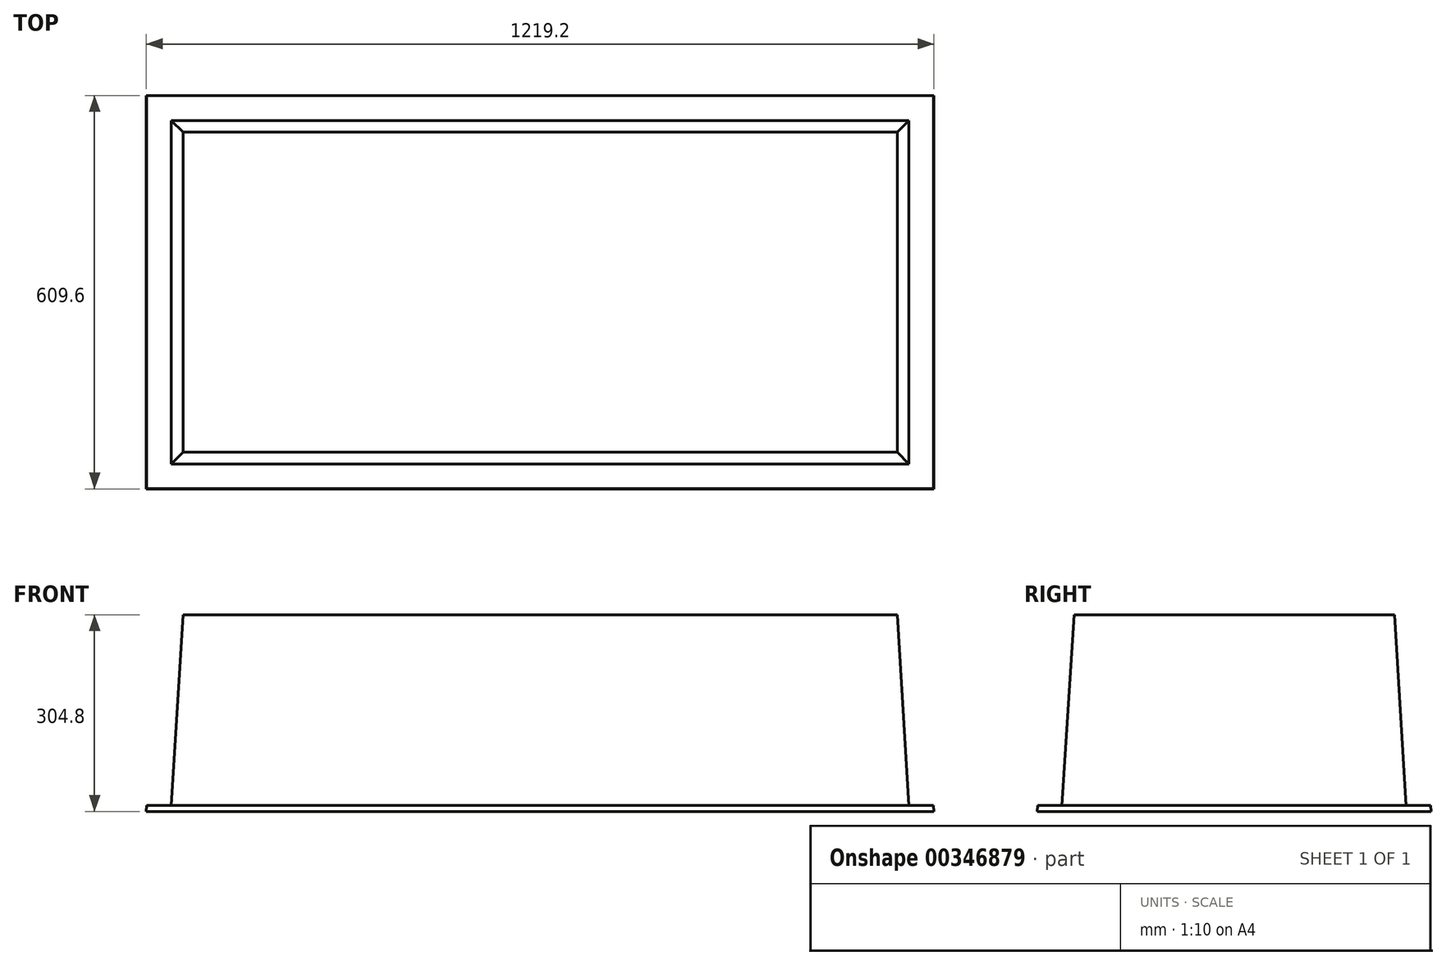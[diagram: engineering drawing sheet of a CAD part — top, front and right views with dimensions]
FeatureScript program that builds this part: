
annotation { "Feature Type Name" : "Feature", "Feature Type Description" : "" }
export const myFeature = defineFeature(function(context is Context, id is Id, definition is map)
    precondition{}
    {
        {
            var Q0;
            Q0=qCreatedBy(makeId("Top.planeOp"),FACE);
            var sketch = newSketch(context, id + "F0", { "sketchPlane" : qUnion([Q0])});
            skLineSegment(sketch, "E0.bottom", {"start": v(0, 0) * mm, "end": v(1219.2, 0) * mm});
            skLineSegment(sketch, "E0.top", {"start": v(0, 609.6) * mm, "end": v(1219.2, 609.6) * mm});
            skLineSegment(sketch, "E0.left", {"start": v(0, 0) * mm, "end": v(0, 609.6) * mm});
            skLineSegment(sketch, "E0.right", {"start": v(1219.2, 0) * mm, "end": v(1219.2, 609.6) * mm});
            skSolve(sketch);
        }
        {
            var Q0;
            Q0=makeQuery(id+"F0.imprint","IMPRINT",FACE,{"disambiguationData":[TD([[makeQuery(id+"F0.imprint","IMPRINT",EDGE,{"derivedFrom":sQuery(id+"F0.wireOp",EDGE,"E0.bottom")}),1.0]])]});
            extrude(context, id + "F1", {"entities" : qUnion([Q0]), "depth" : 304.8 * mm, "hasDraft" : true, "draftAngle" : 3.5 * degree, "draftPullDirection" : true});
        }
        {
            var Q0;
            Q0=qCreatedBy(makeId("Right.planeOp"),FACE);
            var sketch = newSketch(context, id + "F2", { "sketchPlane" : qUnion([Q0])});
            skLineSegment(sketch, "E1", {"start": v(0, 9.53) * mm, "end": v(38.18, 9.53) * mm});
            skLineSegment(sketch, "E2", {"start": v(609.02, 9.52) * mm, "end": v(590.96, 304.8) * mm});
            skLineSegment(sketch, "E3", {"start": v(590.96, 304.8) * mm, "end": v(552.78, 304.8) * mm});
            skLineSegment(sketch, "E4", {"start": v(18.64, 304.8) * mm, "end": v(0, 9.52) * mm});
            skLineSegment(sketch, "E5", {"start": v(570.84, 9.52) * mm, "end": v(552.78, 304.8) * mm});
            skLineSegment(sketch, "E6", {"start": v(38.18, 9.52) * mm, "end": v(56.82, 304.8) * mm});
            skLineSegment(sketch, "E7.trimOffspring", {"start": v(570.84, 9.53) * mm, "end": v(609.02, 9.53) * mm});
            skLineSegment(sketch, "E8.trimOffspring", {"start": v(56.82, 304.8) * mm, "end": v(18.64, 304.8) * mm});
            skSolve(sketch);
        }
        {
            var Q0;
            Q0=makeQuery(id+"F2.imprint","IMPRINT",FACE,{"disambiguationData":[TD([[makeQuery(id+"F2.imprint","IMPRINT",EDGE,{"derivedFrom":sQuery(id+"F2.wireOp",EDGE,"E1")}),1.0]])]});
            var Q1;
            Q1=makeQuery(id+"F2.imprint","IMPRINT",FACE,{"disambiguationData":[TD([[makeQuery(id+"F2.imprint","IMPRINT",EDGE,{"derivedFrom":sQuery(id+"F2.wireOp",EDGE,"E2")}),1.0]])]});
            extrude(context, id + "F3", {"entities" : qUnion([Q0, Q1]), "operationType" : NewBodyOperationType.REMOVE, "endBound" : BoundingType.THROUGH_ALL, "depth" : 25.4 * mm});
        }
        {
            var Q0;
            Q0=qCreatedBy(makeId("Front.planeOp"),FACE);
            var sketch = newSketch(context, id + "F4", { "sketchPlane" : qUnion([Q0])});
            skLineSegment(sketch, "E9", {"start": v(0.58, 9.52) * mm, "end": v(18.64, 304.8) * mm});
            skLineSegment(sketch, "E10", {"start": v(18.64, 304.8) * mm, "end": v(56.81, 304.8) * mm});
            skLineSegment(sketch, "E11", {"start": v(56.81, 304.8) * mm, "end": v(38.75, 9.52) * mm});
            skLineSegment(sketch, "E12", {"start": v(38.75, 9.53) * mm, "end": v(0.58, 9.53) * mm});
            skLineSegment(sketch, "E13", {"start": v(1200.56, 304.8) * mm, "end": v(1162.39, 304.8) * mm});
            skLineSegment(sketch, "E14", {"start": v(1162.39, 304.8) * mm, "end": v(1180.45, 9.53) * mm});
            skLineSegment(sketch, "E15", {"start": v(1180.45, 9.52) * mm, "end": v(1218.62, 9.52) * mm});
            skLineSegment(sketch, "E16", {"start": v(1218.62, 9.53) * mm, "end": v(1200.56, 304.8) * mm});
            skSolve(sketch);
        }
        {
            var Q0;
            Q0=makeQuery(id+"F4.imprint","IMPRINT",FACE,{"disambiguationData":[TD([[makeQuery(id+"F4.imprint","IMPRINT",EDGE,{"derivedFrom":sQuery(id+"F4.wireOp",EDGE,"E9")}),-1.0]])]});
            var Q1;
            Q1=makeQuery(id+"F4.imprint","IMPRINT",FACE,{"disambiguationData":[TD([[makeQuery(id+"F4.imprint","IMPRINT",EDGE,{"derivedFrom":sQuery(id+"F4.wireOp",EDGE,"E13")}),1.0]])]});
            extrude(context, id + "F5", {"entities" : qUnion([Q0, Q1]), "operationType" : NewBodyOperationType.REMOVE, "endBound" : BoundingType.THROUGH_ALL, "oppositeDirection" : true, "depth" : 25.4 * mm});
        }
    });
